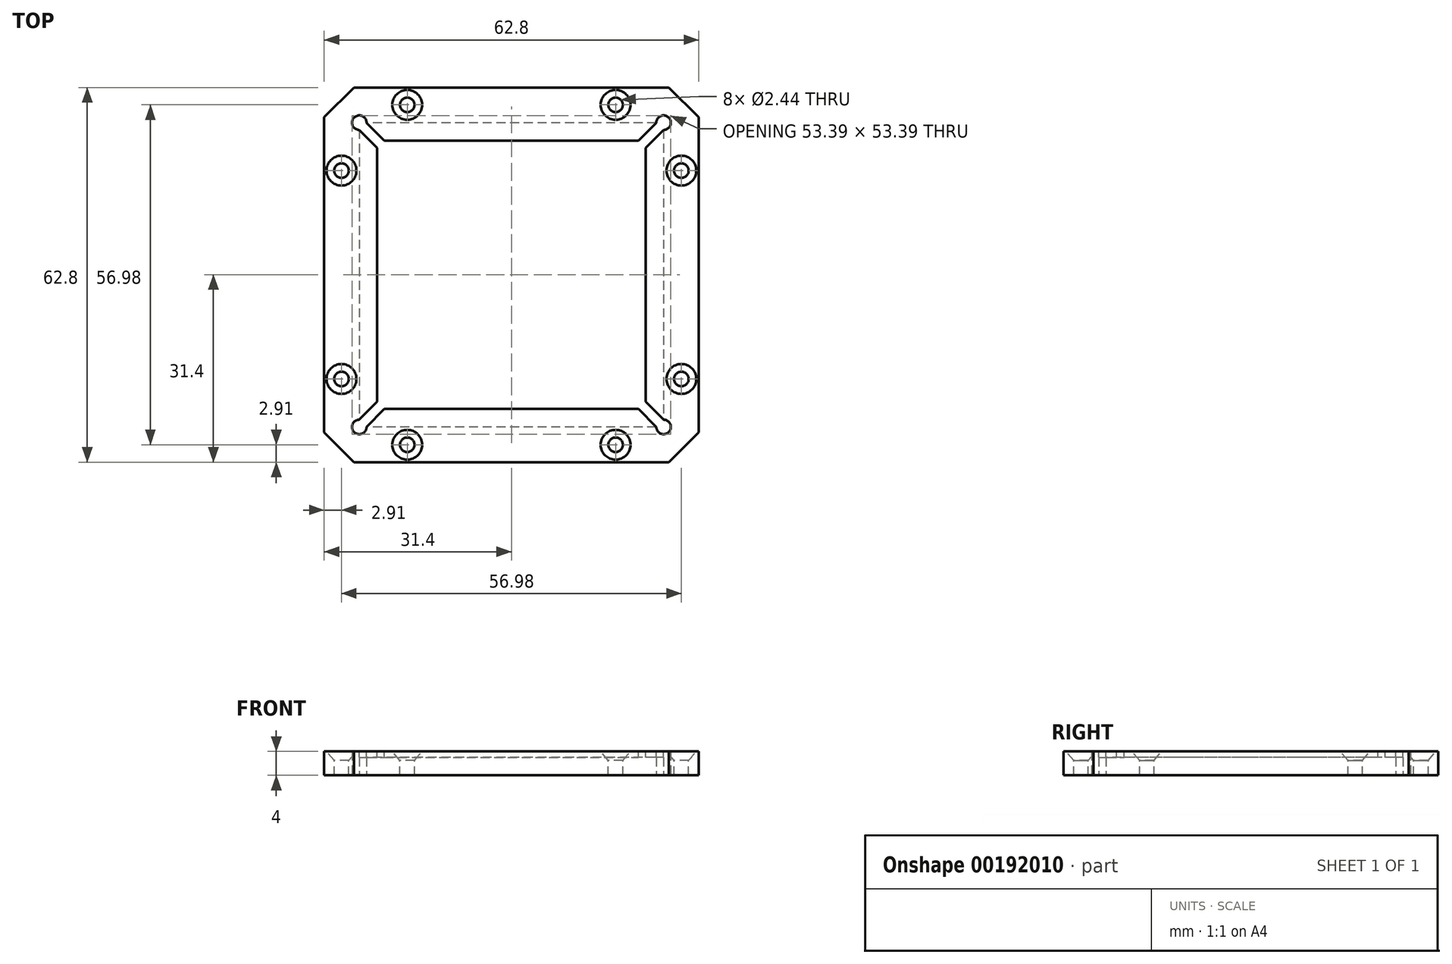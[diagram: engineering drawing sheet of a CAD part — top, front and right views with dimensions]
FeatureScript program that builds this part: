
annotation { "Feature Type Name" : "Feature", "Feature Type Description" : "" }
export const myFeature = defineFeature(function(context is Context, id is Id, definition is map)
    precondition{}
    {
        {
            var Q0;
            Q0=qCreatedBy(makeId("Top.planeOp"),FACE);
            var sketch = newSketch(context, id + "F0", { "sketchPlane" : qUnion([Q0])});
            skLineSegment(sketch, "E0.bottom", {"start": v(31.4, 31.4) * mm, "end": v(-31.4, 31.4) * mm});
            skLineSegment(sketch, "E0.top", {"start": v(31.4, -31.4) * mm, "end": v(-31.4, -31.4) * mm});
            skLineSegment(sketch, "E0.left", {"start": v(31.4, 31.4) * mm, "end": v(31.4, -31.4) * mm});
            skLineSegment(sketch, "E0.right", {"start": v(-31.4, 31.4) * mm, "end": v(-31.4, -31.4) * mm});
            skPoint(sketch, "E0.middle", {"position": v(0, 0) * mm});
            skLineSegment(sketch, "E1.bottom", {"start": v(-22.5, 22.5) * mm, "end": v(22.5, 22.5) * mm});
            skLineSegment(sketch, "E1.top", {"start": v(-22.5, -22.5) * mm, "end": v(22.5, -22.5) * mm});
            skLineSegment(sketch, "E1.left", {"start": v(-22.5, 22.5) * mm, "end": v(-22.5, -22.5) * mm});
            skLineSegment(sketch, "E1.right", {"start": v(22.5, 22.5) * mm, "end": v(22.5, -22.5) * mm});
            skLineSegment(sketch, "E2.bottom", {"start": v(25.5, 25.5) * mm, "end": v(-25.5, 25.5) * mm});
            skLineSegment(sketch, "E2.top", {"start": v(25.5, -25.5) * mm, "end": v(-25.5, -25.5) * mm});
            skLineSegment(sketch, "E2.left", {"start": v(25.5, 25.5) * mm, "end": v(25.5, -25.5) * mm});
            skLineSegment(sketch, "E2.right", {"start": v(-25.5, 25.5) * mm, "end": v(-25.5, -25.5) * mm});
            skPoint(sketch, "E3", {"position": v(-17.46, 28.49) * mm});
            skLineSegment(sketch, "E4", {"start": v(-31.4, 31.4) * mm, "end": v(0, 0) * mm, "construction": true});
            skPoint(sketch, "E5.MirrorP", {"position": v(-28.49, 17.46) * mm});
            skPoint(sketch, "E6.MirrorP", {"position": v(-17.46, -28.49) * mm});
            skPoint(sketch, "E7.MirrorP", {"position": v(-28.49, -17.46) * mm});
            skPoint(sketch, "E8.MirrorP", {"position": v(17.46, 28.49) * mm});
            skPoint(sketch, "E9.MirrorP", {"position": v(28.49, 17.46) * mm});
            skPoint(sketch, "E10.MirrorP", {"position": v(28.49, -17.46) * mm});
            skPoint(sketch, "E11.MirrorP", {"position": v(17.46, -28.49) * mm});
            skPoint(sketch, "E12", {"position": v(-25.5, -25.5) * mm});
            skPoint(sketch, "E13", {"position": v(25.5, -25.5) * mm});
            skPoint(sketch, "E14", {"position": v(-25.5, 25.5) * mm});
            skPoint(sketch, "E15", {"position": v(25.5, 25.5) * mm});
            skSolve(sketch);
        }
        {
            var Q0;
            Q0=makeQuery(id+"F0.imprint","IMPRINT",FACE,{"disambiguationData":[TD([[makeQuery(id+"F0.imprint","IMPRINT",EDGE,{"derivedFrom":sQuery(id+"F0.wireOp",EDGE,"E0.bottom")}),1.0]])]});
            var Q1;
            Q1=makeQuery(id+"F0.imprint","IMPRINT",FACE,{"disambiguationData":[TD([[makeQuery(id+"F0.imprint","IMPRINT",EDGE,{"derivedFrom":sQuery(id+"F0.wireOp",EDGE,"E1.bottom")}),1.0]])]});
            extrude(context, id + "F1", {"entities" : qUnion([Q0, Q1]), "depth" : 4 * mm});
        }
        {
            var Q0;
            Q0=makeQuery(id+"F0.imprint","IMPRINT",FACE,{"disambiguationData":[TD([[makeQuery(id+"F0.imprint","IMPRINT",EDGE,{"derivedFrom":sQuery(id+"F0.wireOp",EDGE,"E1.bottom")}),1.0]])]});
            extrude(context, id + "F2", {"entities" : qUnion([Q0]), "operationType" : NewBodyOperationType.REMOVE, "depth" : 3 * mm});
        }
        {
            var Q0;
            Q0=makeQuery(id+"F1.opExtrude","CAP_FACE",FACE,{"disambiguationData":[OSD([sQuery(id+"F0.wireOp",EDGE,"E0.bottom"),sQuery(id+"F0.wireOp",EDGE,"E0.top"),sQuery(id+"F0.wireOp",EDGE,"E0.left"),sQuery(id+"F0.wireOp",EDGE,"E0.right"),sQuery(id+"F0.wireOp",EDGE,"E1.bottom"),sQuery(id+"F0.wireOp",EDGE,"E1.top"),sQuery(id+"F0.wireOp",EDGE,"E1.left"),sQuery(id+"F0.wireOp",EDGE,"E1.right")])],"isStart":false});
            var sketch = newSketch(context, id + "F3", { "sketchPlane" : qUnion([Q0])});
            skPoint(sketch, "E16.0", {"position": v(-17.46, 28.49) * mm});
            skPoint(sketch, "E17.0", {"position": v(17.46, 28.49) * mm});
            skPoint(sketch, "E18.0", {"position": v(28.49, 17.46) * mm});
            skPoint(sketch, "E19.0", {"position": v(28.49, -17.46) * mm});
            skPoint(sketch, "E20.0", {"position": v(17.46, -28.49) * mm});
            skPoint(sketch, "E21.0", {"position": v(-17.46, -28.49) * mm});
            skPoint(sketch, "E22.0", {"position": v(-28.49, -17.46) * mm});
            skPoint(sketch, "E23.0", {"position": v(-28.49, 17.46) * mm});
            skSolve(sketch);
        }
        {
            var Q0;
            Q0=sQuery(id+"F3.wireOp",VERTEX,"E21.0");
            var Q1;
            Q1=sQuery(id+"F3.wireOp",VERTEX,"E22.0");
            var Q2;
            Q2=sQuery(id+"F3.wireOp",VERTEX,"E23.0");
            var Q3;
            Q3=sQuery(id+"F3.wireOp",VERTEX,"E16.0");
            var Q4;
            Q4=sQuery(id+"F3.wireOp",VERTEX,"E17.0");
            var Q5;
            Q5=sQuery(id+"F3.wireOp",VERTEX,"E18.0");
            var Q6;
            Q6=sQuery(id+"F3.wireOp",VERTEX,"E19.0");
            var Q7;
            Q7=sQuery(id+"F3.wireOp",VERTEX,"E20.0");
            var Q8;
            Q8=makeQuery(id+"F1.opExtrude","SWEPT_BODY",BODY,{"disambiguationData":[OSD([sQuery(id+"F0.wireOp",EDGE,"E0.bottom"),sQuery(id+"F0.wireOp",EDGE,"E0.top"),sQuery(id+"F0.wireOp",EDGE,"E0.left"),sQuery(id+"F0.wireOp",EDGE,"E0.right"),sQuery(id+"F0.wireOp",EDGE,"E1.bottom"),sQuery(id+"F0.wireOp",EDGE,"E1.top"),sQuery(id+"F0.wireOp",EDGE,"E1.left"),sQuery(id+"F0.wireOp",EDGE,"E1.right")])]});
            hole(context, id + "F4", {"style" : HoleStyle.C_SINK, "endStyle" : HoleEndStyle.BLIND, "standardTappedOrClearance" : lookupTablePath({ "standard" : "ANSI", "fit" : "Normal (ASME)", "size" : "#2", "type" : "Clearance" }), "standardBlindInLast" : lookupTablePath({ "fit" : "Free", "standard" : "ANSI", "size" : "#2", "type" : "Clearance" }), "holeDiameter" : 2.44 * mm, "cSinkDiameter" : 5 * mm, "cSinkAngle" : 82 * degree, "holeDepth" : 20 * mm, "locations" : qUnion([Q0, Q1, Q2, Q3, Q4, Q5, Q6, Q7]), "scope" : qUnion([Q8])});
        }
        {
            var Q0;
            Q0=sQuery(id+"F0.wireOp",VERTEX,"E14");
            var Q1;
            Q1=sQuery(id+"F0.wireOp",VERTEX,"E15");
            var Q2;
            Q2=sQuery(id+"F0.wireOp",VERTEX,"E12");
            var Q3;
            Q3=sQuery(id+"F0.wireOp",VERTEX,"E13");
            var Q4;
            Q4=makeQuery(id+"F1.opExtrude","SWEPT_BODY",BODY,{"disambiguationData":[OSD([sQuery(id+"F0.wireOp",EDGE,"E0.bottom"),sQuery(id+"F0.wireOp",EDGE,"E0.top"),sQuery(id+"F0.wireOp",EDGE,"E0.left"),sQuery(id+"F0.wireOp",EDGE,"E0.right"),sQuery(id+"F0.wireOp",EDGE,"E1.bottom"),sQuery(id+"F0.wireOp",EDGE,"E1.top"),sQuery(id+"F0.wireOp",EDGE,"E1.left"),sQuery(id+"F0.wireOp",EDGE,"E1.right")])]});
            hole(context, id + "F5", {"style" : HoleStyle.SIMPLE, "endStyle" : HoleEndStyle.BLIND, "oppositeDirection" : true, "standardTappedOrClearance" : lookupTablePath({ "standard" : "ANSI", "fit" : "Normal (ASME)", "size" : "#2", "type" : "Clearance" }), "standardBlindInLast" : lookupTablePath({ "fit" : "Free", "standard" : "ANSI", "size" : "#2", "type" : "Clearance" }), "holeDiameter" : 2.44 * mm, "holeDepth" : 20 * mm, "locations" : qUnion([Q0, Q1, Q2, Q3]), "scope" : qUnion([Q4])});
        }
        {
            var Q0;
            Q0=makeQuery(id+"F1.opExtrude","CAP_FACE",FACE,{"disambiguationData":[OSD([sQuery(id+"F0.wireOp",EDGE,"E0.bottom"),sQuery(id+"F0.wireOp",EDGE,"E0.top"),sQuery(id+"F0.wireOp",EDGE,"E0.left"),sQuery(id+"F0.wireOp",EDGE,"E0.right"),sQuery(id+"F0.wireOp",EDGE,"E1.bottom"),sQuery(id+"F0.wireOp",EDGE,"E1.top"),sQuery(id+"F0.wireOp",EDGE,"E1.left"),sQuery(id+"F0.wireOp",EDGE,"E1.right")])],"isStart":false});
            var sketch = newSketch(context, id + "F6", { "sketchPlane" : qUnion([Q0])});
            skLineSegment(sketch, "E24.0.0", {"start": v(25.5, -25.5) * mm, "end": v(25.5, 25.5) * mm});
            skLineSegment(sketch, "E24.0.1", {"start": v(25.5, 25.5) * mm, "end": v(-25.5, 25.5) * mm});
            skLineSegment(sketch, "E24.0.2", {"start": v(-25.5, 25.5) * mm, "end": v(-25.5, -25.5) * mm});
            skLineSegment(sketch, "E24.0.3", {"start": v(-25.5, -25.5) * mm, "end": v(25.5, -25.5) * mm});
            skLineSegment(sketch, "E25.0.0", {"start": v(22.5, 22.5) * mm, "end": v(-22.5, 22.5) * mm});
            skLineSegment(sketch, "E25.0.1", {"start": v(-22.5, 22.5) * mm, "end": v(-22.5, -22.5) * mm});
            skLineSegment(sketch, "E25.0.2", {"start": v(-22.5, -22.5) * mm, "end": v(22.5, -22.5) * mm});
            skLineSegment(sketch, "E25.0.3", {"start": v(22.5, -22.5) * mm, "end": v(22.5, 22.5) * mm});
            skArc(sketch, "E26.0", {"start": v(-24.28, -25.5) * mm, "mid": v(-26.36, -26.36) * mm, "end": v(-25.5, -24.28) * mm});
            skArc(sketch, "E27.0", {"start": v(25.5, -24.28) * mm, "mid": v(26.36, -26.36) * mm, "end": v(24.28, -25.5) * mm});
            skArc(sketch, "E28.0", {"start": v(24.28, 25.5) * mm, "mid": v(26.36, 26.36) * mm, "end": v(25.5, 24.28) * mm});
            skArc(sketch, "E29.0", {"start": v(-25.5, 24.28) * mm, "mid": v(-26.36, 26.36) * mm, "end": v(-24.28, 25.5) * mm});
            skLineSegment(sketch, "E30", {"start": v(-24.28, -25.5) * mm, "end": v(-21.28, -22.5) * mm});
            skLineSegment(sketch, "E31", {"start": v(-25.5, -24.28) * mm, "end": v(-22.5, -21.28) * mm});
            skLineSegment(sketch, "E32.MirrorCS", {"start": v(24.28, -25.5) * mm, "end": v(21.28, -22.5) * mm});
            skLineSegment(sketch, "E33.MirrorCS", {"start": v(25.5, -24.28) * mm, "end": v(22.5, -21.28) * mm});
            skLineSegment(sketch, "E34.MirrorCS", {"start": v(-24.28, 25.5) * mm, "end": v(-21.28, 22.5) * mm});
            skLineSegment(sketch, "E35.MirrorCS", {"start": v(-25.5, 24.28) * mm, "end": v(-22.5, 21.28) * mm});
            skLineSegment(sketch, "E36.MirrorCS", {"start": v(24.28, 25.5) * mm, "end": v(21.28, 22.5) * mm});
            skLineSegment(sketch, "E37.MirrorCS", {"start": v(25.5, 24.28) * mm, "end": v(22.5, 21.28) * mm});
            skSolve(sketch);
        }
        {
            var Q0;
            {var subQ1=sQuery(id+"F6.wireOp",EDGE,"E34.MirrorCS");Q0=makeQuery(id+"F6.imprint","IMPRINT",FACE,{"disambiguationData":[TD([[makeQuery(id+"F6.imprint","IMPRINT",EDGE,{"derivedFrom":subQ1}),-1.0]])]});}
            var Q1;
            {var subQ1=sQuery(id+"F6.wireOp",EDGE,"E36.MirrorCS");Q1=makeQuery(id+"F6.imprint","IMPRINT",FACE,{"disambiguationData":[TD([[makeQuery(id+"F6.imprint","IMPRINT",EDGE,{"derivedFrom":subQ1}),1.0]])]});}
            var Q2;
            {var subQ0=sQuery(id+"F6.wireOp",EDGE,"E30");Q2=makeQuery(id+"F6.imprint","IMPRINT",FACE,{"disambiguationData":[TD([[makeQuery(id+"F6.imprint","IMPRINT",EDGE,{"derivedFrom":subQ0}),1.0]])]});}
            var Q3;
            {var subQ4=sQuery(id+"F6.wireOp",EDGE,"E32.MirrorCS");Q3=makeQuery(id+"F6.imprint","IMPRINT",FACE,{"disambiguationData":[TD([[makeQuery(id+"F6.imprint","IMPRINT",EDGE,{"derivedFrom":subQ4}),-1.0]])]});}
            extrude(context, id + "F7", {"entities" : qUnion([Q0, Q1, Q2, Q3]), "operationType" : NewBodyOperationType.REMOVE, "endBound" : BoundingType.THROUGH_ALL, "oppositeDirection" : true, "depth" : 25 * mm});
        }
        {
            var Q0;
            Q0=makeQuery(id+"F1.opExtrude","SWEPT_EDGE",EDGE,{"disambiguationData":[OSD([sQuery(id+"F0.wireOp",EDGE,"E0.top"),sQuery(id+"F0.wireOp",EDGE,"E0.left")])]});
            var Q1;
            Q1=makeQuery(id+"F1.opExtrude","SWEPT_EDGE",EDGE,{"disambiguationData":[OSD([sQuery(id+"F0.wireOp",EDGE,"E0.top"),sQuery(id+"F0.wireOp",EDGE,"E0.right")])]});
            var Q2;
            Q2=makeQuery(id+"F1.opExtrude","SWEPT_EDGE",EDGE,{"disambiguationData":[OSD([sQuery(id+"F0.wireOp",EDGE,"E0.bottom"),sQuery(id+"F0.wireOp",EDGE,"E0.right")])]});
            var Q3;
            Q3=makeQuery(id+"F1.opExtrude","SWEPT_EDGE",EDGE,{"disambiguationData":[OSD([sQuery(id+"F0.wireOp",EDGE,"E0.bottom"),sQuery(id+"F0.wireOp",EDGE,"E0.left")])]});
            chamfer(context, id + "F8", {"entities" : qUnion([Q0, Q1, Q2, Q3]), "width" : 5 * mm, "tangentPropagation" : true});
        }
    });
